# Revit family: TataSteel_Lintels_CG_130-145_125-140
name_source: partatom
category: Generic Models
revit_build: Autodesk Revit 2015 (Build: 20140606_1530(x64)
units: mm (PartAtom-declared; Revit-internal decimal feet)

## types (1)
- TataSteel_Lintels_CG_130-145_125-140
    AllowableLoadLimiting = 26 mm
    AssetType = FIXED
    BIMObjectName = TataSteel_Lintel_CG130_125_3000
    BIMobject category = Beams & Lintels
    CharacteristicDeflectionUnderLoad = 0 mm  [stored 0 ft]
    CharacteristicResistanceToFire = 60 mm  [stored 0.19685 ft]
    CharacteristicThermalConductivity = 0 mm  [stored 0 ft]
    Color = Black
    Date of publishing = 7/15/2016
    Description = Standard duty cavity wall lintel
    Edition number = 1
    ExpectedLife = 60 yrs
    Finish = Galv and Powder coated
    FireRating = 60
    Grade = DX51
    IFC Classification = Structural Member
    IfcExportAs = IfcBeamType
    IfcExportType = LINTEL
    Installation instructions = http://catnic.com
    InstallationDate = 1900-12-31T23:59:59
    IsExternal = No
    LengthIncrement = 150mm up to 3000mm. 
300mm above 3000mm
    LintelCavity = 128 mm  [stored 0.419948 ft]
    LintelFace = 116 mm  [stored 0.380577 ft]
    LintelHeight = 220 mm  [stored 0.721785 ft]
    LintelInnerLeaf = 125 mm  [stored 0.410105 ft]
    LintelInsulation = Insulation
    LintelLength = 3000 mm  [stored 9.84252 ft]
    LintelLip = 2 mm  [stored 0.00656168 ft]
    LintelMaterial = Steel
    LintelOuterLeaf = 95 mm
    LintelThickness = 3 mm  [stored 0.00984252 ft]
    LintelTop = 10 mm  [stored 0.0328084 ft]
    LintelType = CAVITY
    LoadBearing = No
    LoadCategory = STANDARD DUTY
    Manufacturer = Catnic, TATA
    Manufacturer country = United Kingdom
    Manufacturer name = Tata Steel
    ManufacturerURL = www.catnic.com
    Material = Galvanised Steel
    Material main = Steel
    MaxLintelLength = 3600mm for a 100mm inner leaf. 
3000mm for a 125mm inner leaf
    MinLintelLength = 750
    Model = TataSteel_Lintel_CG130_125_3000
    ModelNumber = CG
    ModelReference = Cavity Walls
    NBSDescription = Pre fabricated Steel Lintel
    NBSReference = F30 755
    Name = Lintel
    Nominal height = 0
    Nominal width = 0
    NominalLength = 3000 mm  [stored 9.84252 ft]
    OmniClass Code = 23-13 21 25 11
    OmniClass Description = Lintels
    Product Guid = 0836c148-5d47-4569-beb7-ec558f593e9c
    Product SKU = catnic-cg
    Product certification = http://catnic.com
    Product family = Lintels
    Product group = Catnic
    ProductInformation = www.catnic.com
    QR code = http://bimobject.com
    Roll = 0 mm  [stored 0 ft]
    SafeWorkingLoad = 26 mm
    Shape = Open back lintel
    Size = 220H x348W x3000L
    Slope = 0 mm  [stored 0 ft]
    Span = 2700 mm  [stored 8.85827 ft]
    TSE_BIMObjectName = TataSteel_Lintel_CG130_125_3000
    TSE_Description = Catnic CG lintels use unique, discrete brackets in place of a base.
Depending on the wall construction, they can have a linear thermal
transmittance ψ value of less than 0.21 W/mK.
    TSE_Documentation = www.catnic.com
    TSE_InstallationInstructions = www.catnic.com
    TSE_ManufacturerURL = www.catnic.com
    TSE_Model = TataSteel_Lintel_CG130_125_3000
    TSE_ProductCertification = www.catnic.com
    TSE_QR code = <None>
    Technical description = http://catnic.com
    ThermalTransmittance = 0 mm  [stored 0 ft]
    UNSPSC Code = 30101704
    URL = www.catnic.com
    Uniclass 1.4 Code = L3241
    Uniclass 1.4 Description = Lintels
    Uniclass 2015 Code = Pr_20_85_48
    Uniclass 2015 Name = Lintels
    Uniclass2015 = Pr_20_85_48_11
    WallCavityRange = 130-145
    WallInnerLeafRange = 125-140
    WarrantyStartDate = 1900-12-31T23:59:59
    Weight = 14 mm  [stored 0.0459318 ft]
    Weight Net (Kg) = 0
    b1 = 159 mm  [stored 0.521654 ft]
    b2 = 189 mm  [stored 0.620079 ft]
    b3 = 64 mm  [stored 0.209974 ft]

note: [stored X ft] marks values corroborated as IEEE doubles in the binary element streams (Revit-internal decimal feet)

## geometry (parser evidence)
native form markers: Sweep x2
no freeform markers — native parametric forms only
